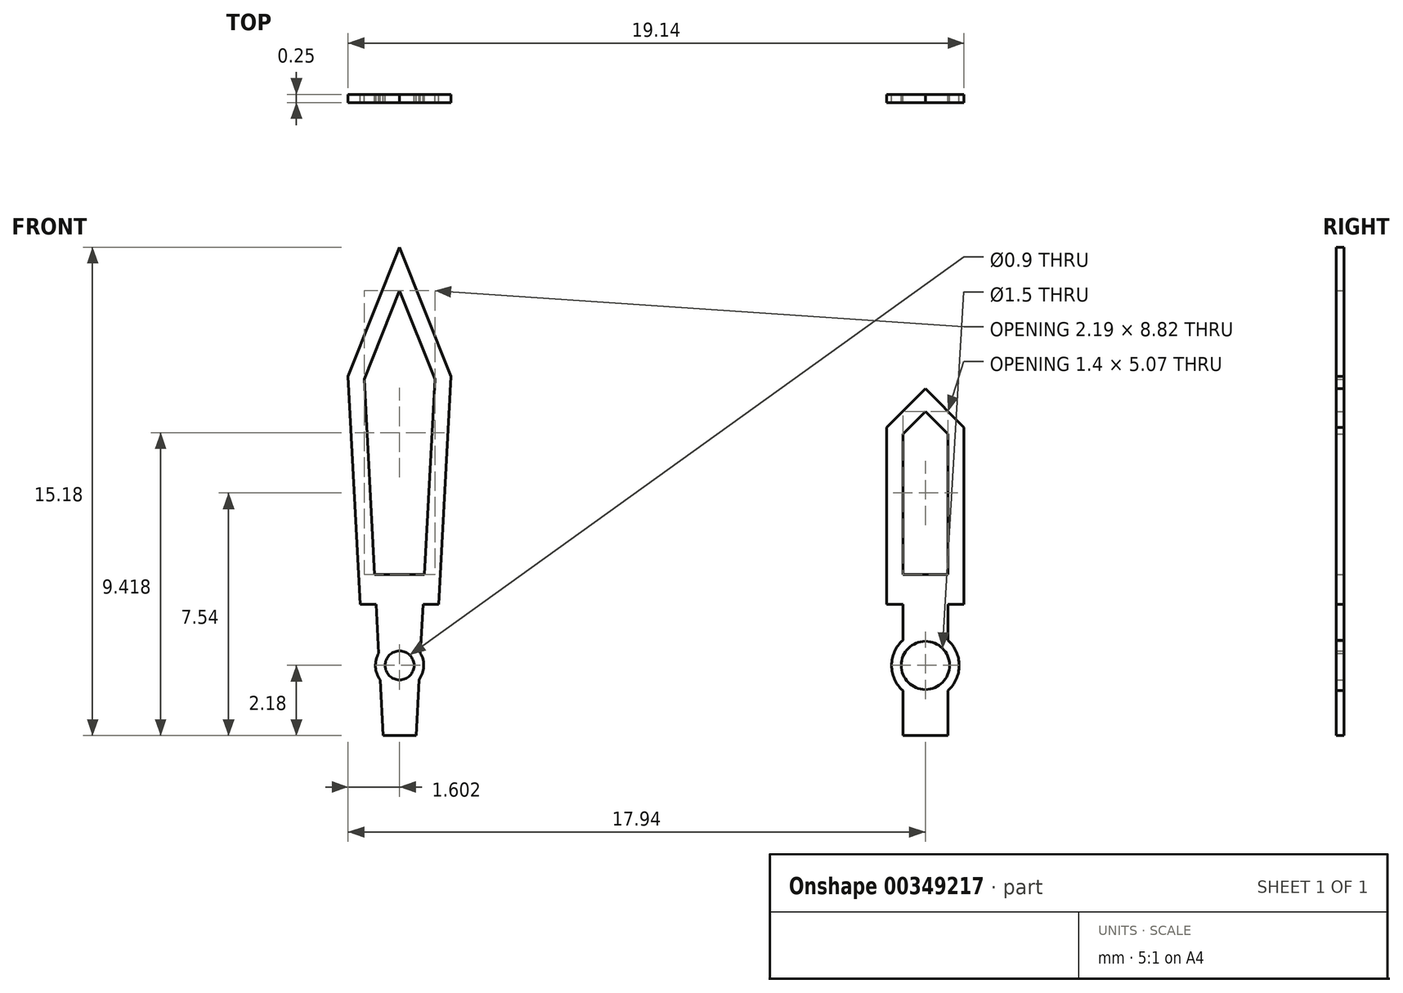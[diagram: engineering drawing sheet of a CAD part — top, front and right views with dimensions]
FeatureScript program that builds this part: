
annotation { "Feature Type Name" : "Feature", "Feature Type Description" : "" }
export const myFeature = defineFeature(function(context is Context, id is Id, definition is map)
    precondition{}
    {
        {
            var Q0;
            Q0=qCreatedBy(makeId("Front.planeOp"),FACE);
            var sketch = newSketch(context, id + "F0", { "sketchPlane" : qUnion([Q0])});
            skLineSegment(sketch, "E0", {"start": v(-36.59, 13) * mm, "end": v(-34.99, 8.98) * mm});
            skCircle(sketch, "E1", {"center": v(-36.59, 0) * mm, "radius": 0.45 * mm});
            skCircle(sketch, "E2.0", {"center": v(-36.59, 0) * mm, "radius": 0.75 * mm});
            skCircle(sketch, "E3", {"center": v(-20.25, 0) * mm, "radius": 0.75 * mm});
            skCircle(sketch, "E4", {"center": v(-20.25, 0) * mm, "radius": 1.05 * mm});
            skLineSegment(sketch, "E5", {"start": v(-36.59, 13) * mm, "end": v(-36.59, 0) * mm});
            skLineSegment(sketch, "E6.MirrorCS", {"start": v(-36.59, 13) * mm, "end": v(-38.19, 8.98) * mm});
            skLineSegment(sketch, "E7", {"start": v(-20.25, 8.6) * mm, "end": v(-20.25, 0) * mm});
            skLineSegment(sketch, "E8", {"start": v(-34.99, 8.98) * mm, "end": v(-35.58, -2.18) * mm});
            skLineSegment(sketch, "E9.MirrorCS", {"start": v(-38.19, 8.98) * mm, "end": v(-37.6, -2.18) * mm});
            skLineSegment(sketch, "E10", {"start": v(-19.05, 7.4) * mm, "end": v(-20.25, 8.6) * mm});
            skLineSegment(sketch, "E11", {"start": v(-20.25, 7.9) * mm, "end": v(-19.55, 7.2) * mm});
            skLineSegment(sketch, "E12.MirrorCS", {"start": v(-20.25, 7.9) * mm, "end": v(-20.95, 7.2) * mm});
            skLineSegment(sketch, "E13.MirrorCS", {"start": v(-21.45, 7.4) * mm, "end": v(-20.25, 8.6) * mm});
            skLineSegment(sketch, "E14", {"start": v(-36.59, 11.65) * mm, "end": v(-35.5, 8.9) * mm});
            skLineSegment(sketch, "E15", {"start": v(-35.5, 8.9) * mm, "end": v(-35.94, 0.38) * mm});
            skLineSegment(sketch, "E16.MirrorCS", {"start": v(-36.59, 11.65) * mm, "end": v(-37.68, 8.9) * mm});
            skLineSegment(sketch, "E17.MirrorCS", {"start": v(-37.68, 8.9) * mm, "end": v(-37.23, 0.38) * mm});
            skLineSegment(sketch, "E18", {"start": v(-19.05, 2.83) * mm, "end": v(-21.45, 2.83) * mm});
            skLineSegment(sketch, "E19.0", {"start": v(-19.05, -2.18) * mm, "end": v(-21.45, -2.18) * mm});
            skLineSegment(sketch, "E20", {"start": v(-21.45, 7.4) * mm, "end": v(-21.45, -2.18) * mm});
            skLineSegment(sketch, "E21", {"start": v(-20.95, 7.2) * mm, "end": v(-20.95, 0.27) * mm});
            skLineSegment(sketch, "E22", {"start": v(-19.05, 7.4) * mm, "end": v(-19.05, -2.18) * mm});
            skLineSegment(sketch, "E23", {"start": v(-19.55, 7.2) * mm, "end": v(-19.55, 0.27) * mm});
            skLineSegment(sketch, "E24.trimOffspring", {"start": v(-35.32, 2.83) * mm, "end": v(-37.86, 2.83) * mm});
            skLineSegment(sketch, "E25.trimOffspring", {"start": v(-35.58, -2.18) * mm, "end": v(-37.95, -2.18) * mm});
            skLineSegment(sketch, "E26.trimOffspring", {"start": v(-20.95, -0.27) * mm, "end": v(-20.95, -2.18) * mm});
            skLineSegment(sketch, "E27.trimOffspring", {"start": v(-19.55, -0.27) * mm, "end": v(-19.55, -2.18) * mm});
            skLineSegment(sketch, "E28.trimOffspring", {"start": v(-37.2, -0.45) * mm, "end": v(-37.1, -2.18) * mm});
            skLineSegment(sketch, "E29.trimOffspring", {"start": v(-35.99, -0.45) * mm, "end": v(-36.08, -2.18) * mm});
            skLineSegment(sketch, "E30.0", {"start": v(-35.58, -1.68) * mm, "end": v(-37.95, -1.68) * mm});
            skLineSegment(sketch, "E31.0", {"start": v(-19.05, -1.68) * mm, "end": v(-21.45, -1.68) * mm});
            skLineSegment(sketch, "E32", {"start": v(-19.05, 1.9) * mm, "end": v(-37.8, 1.9) * mm});
            skLineSegment(sketch, "E33", {"start": v(-35.32, 2.83) * mm, "end": v(-21.45, 2.83) * mm});
            skSolve(sketch);
        }
        {
            var Q0;
            {var subQ0=sQuery(id+"F0.wireOp",EDGE,"E28.trimOffspring");var subQ1=sQuery(id+"F0.wireOp",EDGE,"E25.trimOffspring");var subQ2=makeQuery(id+"F0.imprint","INTERSECT",VERTEX,{"derivedFrom":[subQ1,subQ0]});Q0=makeQuery(id+"F0.imprint","IMPRINT",FACE,{"disambiguationData":[TD([[makeQuery(id+"F0.imprint","IMPRINT",EDGE,{"disambiguationData":[TD([[subQ2,1.0]])],"derivedFrom":subQ1}),-1.0]])]});}
            var Q1;
            {var subQ2=sQuery(id+"F0.wireOp",EDGE,"E0");Q1=makeQuery(id+"F0.imprint","IMPRINT",FACE,{"disambiguationData":[TD([[makeQuery(id+"F0.imprint","IMPRINT",EDGE,{"derivedFrom":subQ2}),-1.0]])]});}
            var Q2;
            {var subQ0=sQuery(id+"F0.wireOp",EDGE,"E6.MirrorCS");Q2=makeQuery(id+"F0.imprint","IMPRINT",FACE,{"disambiguationData":[TD([[makeQuery(id+"F0.imprint","IMPRINT",EDGE,{"derivedFrom":subQ0}),1.0]])]});}
            var Q3;
            {var subQ5=sQuery(id+"F0.wireOp",EDGE,"E10");Q3=makeQuery(id+"F0.imprint","IMPRINT",FACE,{"disambiguationData":[TD([[makeQuery(id+"F0.imprint","IMPRINT",EDGE,{"derivedFrom":subQ5}),1.0]])]});}
            var Q4;
            {var subQ5=sQuery(id+"F0.wireOp",EDGE,"E12.MirrorCS");Q4=makeQuery(id+"F0.imprint","IMPRINT",FACE,{"disambiguationData":[TD([[makeQuery(id+"F0.imprint","IMPRINT",EDGE,{"derivedFrom":subQ5}),-1.0]])]});}
            var Q5;
            Q5=makeQuery(id+"F0.imprint","IMPRINT",FACE,{"disambiguationData":[TD([[makeQuery(id+"F0.imprint","IMPRINT",EDGE,{"derivedFrom":sQuery(id+"F0.wireOp",EDGE,"E1")}),-1.0]])]});
            var Q6;
            {var subQ0=sQuery(id+"F0.wireOp",EDGE,"E23");var subQ1=sQuery(id+"F0.wireOp",EDGE,"E3");var subQ2=makeQuery(id+"F0.imprint","INTERSECT",VERTEX,{"derivedFrom":[subQ1,subQ0]});Q6=makeQuery(id+"F0.imprint","IMPRINT",FACE,{"disambiguationData":[TD([[makeQuery(id+"F0.imprint","IMPRINT",EDGE,{"disambiguationData":[TD([[subQ2,-1.0]])],"derivedFrom":subQ1}),-1.0]])]});}
            var Q7;
            {var subQ0=sQuery(id+"F0.wireOp",EDGE,"E21");var subQ1=sQuery(id+"F0.wireOp",EDGE,"E3");var subQ2=makeQuery(id+"F0.imprint","INTERSECT",VERTEX,{"derivedFrom":[subQ1,subQ0]});Q7=makeQuery(id+"F0.imprint","IMPRINT",FACE,{"disambiguationData":[TD([[makeQuery(id+"F0.imprint","IMPRINT",EDGE,{"disambiguationData":[TD([[subQ2,1.0]])],"derivedFrom":subQ1}),-1.0]])]});}
            var Q8;
            {var subQ0=sQuery(id+"F0.wireOp",EDGE,"E21");var subQ1=sQuery(id+"F0.wireOp",EDGE,"E3");var subQ2=makeQuery(id+"F0.imprint","INTERSECT",VERTEX,{"derivedFrom":[subQ1,subQ0]});Q8=makeQuery(id+"F0.imprint","IMPRINT",FACE,{"disambiguationData":[TD([[makeQuery(id+"F0.imprint","IMPRINT",EDGE,{"disambiguationData":[TD([[subQ2,-1.0]])],"derivedFrom":subQ1}),-1.0]])]});}
            var Q9;
            {var subQ0=sQuery(id+"F0.wireOp",EDGE,"E26.trimOffspring");var subQ1=sQuery(id+"F0.wireOp",EDGE,"E3");var subQ2=makeQuery(id+"F0.imprint","INTERSECT",VERTEX,{"derivedFrom":[subQ1,subQ0]});Q9=makeQuery(id+"F0.imprint","IMPRINT",FACE,{"disambiguationData":[TD([[makeQuery(id+"F0.imprint","IMPRINT",EDGE,{"disambiguationData":[TD([[subQ2,-1.0]])],"derivedFrom":subQ1}),-1.0]])]});}
            var Q10;
            {var subQ0=sQuery(id+"F0.wireOp",EDGE,"E23");var subQ1=sQuery(id+"F0.wireOp",EDGE,"E3");var subQ2=makeQuery(id+"F0.imprint","INTERSECT",VERTEX,{"derivedFrom":[subQ1,subQ0]});Q10=makeQuery(id+"F0.imprint","IMPRINT",FACE,{"disambiguationData":[TD([[makeQuery(id+"F0.imprint","IMPRINT",EDGE,{"disambiguationData":[TD([[subQ2,1.0]])],"derivedFrom":subQ1}),-1.0]])]});}
            var Q11;
            {var subQ0=sQuery(id+"F0.wireOp",EDGE,"E26.trimOffspring");var subQ1=sQuery(id+"F0.wireOp",EDGE,"E19.0");var subQ2=makeQuery(id+"F0.imprint","INTERSECT",VERTEX,{"derivedFrom":[subQ1,subQ0]});Q11=makeQuery(id+"F0.imprint","IMPRINT",FACE,{"disambiguationData":[TD([[makeQuery(id+"F0.imprint","IMPRINT",EDGE,{"disambiguationData":[TD([[subQ2,1.0]])],"derivedFrom":subQ1}),-1.0]])]});}
            var Q12;
            {var subQ0=sQuery(id+"F0.wireOp",EDGE,"E28.trimOffspring");var subQ1=sQuery(id+"F0.wireOp",EDGE,"E2.0");var subQ2=makeQuery(id+"F0.imprint","INTERSECT",VERTEX,{"derivedFrom":[subQ1,subQ0]});Q12=makeQuery(id+"F0.imprint","IMPRINT",FACE,{"disambiguationData":[TD([[makeQuery(id+"F0.imprint","IMPRINT",EDGE,{"disambiguationData":[TD([[subQ2,-1.0]])],"derivedFrom":subQ1}),-1.0]])]});}
            var Q13;
            {var subQ0=sQuery(id+"F0.wireOp",EDGE,"E15");var subQ1=sQuery(id+"F0.wireOp",EDGE,"E2.0");var subQ2=makeQuery(id+"F0.imprint","INTERSECT",VERTEX,{"derivedFrom":[subQ1,subQ0]});Q13=makeQuery(id+"F0.imprint","IMPRINT",FACE,{"disambiguationData":[TD([[makeQuery(id+"F0.imprint","IMPRINT",EDGE,{"disambiguationData":[TD([[subQ2,-1.0]])],"derivedFrom":subQ1}),-1.0]])]});}
            var Q14;
            {var subQ0=sQuery(id+"F0.wireOp",EDGE,"E17.MirrorCS");var subQ1=sQuery(id+"F0.wireOp",EDGE,"E2.0");var subQ2=makeQuery(id+"F0.imprint","INTERSECT",VERTEX,{"derivedFrom":[subQ1,subQ0]});Q14=makeQuery(id+"F0.imprint","IMPRINT",FACE,{"disambiguationData":[TD([[makeQuery(id+"F0.imprint","IMPRINT",EDGE,{"disambiguationData":[TD([[subQ2,1.0]])],"derivedFrom":subQ1}),-1.0]])]});}
            var Q15;
            {var subQ0=sQuery(id+"F0.wireOp",EDGE,"E26.trimOffspring");var subQ1=sQuery(id+"F0.wireOp",EDGE,"E4");var subQ2=makeQuery(id+"F0.imprint","INTERSECT",VERTEX,{"derivedFrom":[subQ1,subQ0]});Q15=makeQuery(id+"F0.imprint","IMPRINT",FACE,{"disambiguationData":[TD([[makeQuery(id+"F0.imprint","IMPRINT",EDGE,{"disambiguationData":[TD([[subQ2,-1.0]])],"derivedFrom":subQ1}),-1.0]])]});}
            var Q16;
            {var subQ0=sQuery(id+"F0.wireOp",EDGE,"E7");var subQ1=sQuery(id+"F0.wireOp",EDGE,"E4");var subQ2=makeQuery(id+"F0.imprint","INTERSECT",VERTEX,{"derivedFrom":[subQ1,subQ0]});Q16=makeQuery(id+"F0.imprint","IMPRINT",FACE,{"disambiguationData":[TD([[makeQuery(id+"F0.imprint","IMPRINT",EDGE,{"disambiguationData":[TD([[subQ2,1.0]])],"derivedFrom":subQ1}),-1.0]])]});}
            var Q17;
            {var subQ0=sQuery(id+"F0.wireOp",EDGE,"E7");var subQ1=sQuery(id+"F0.wireOp",EDGE,"E4");var subQ2=makeQuery(id+"F0.imprint","INTERSECT",VERTEX,{"derivedFrom":[subQ1,subQ0]});Q17=makeQuery(id+"F0.imprint","IMPRINT",FACE,{"disambiguationData":[TD([[makeQuery(id+"F0.imprint","IMPRINT",EDGE,{"disambiguationData":[TD([[subQ2,-1.0]])],"derivedFrom":subQ1}),-1.0]])]});}
            var Q18;
            {var subQ0=sQuery(id+"F0.wireOp",EDGE,"E24.trimOffspring");var subQ1=sQuery(id+"F0.wireOp",EDGE,"E9.MirrorCS");var subQ2=makeQuery(id+"F0.imprint","INTERSECT",VERTEX,{"derivedFrom":[subQ1,subQ0]});Q18=makeQuery(id+"F0.imprint","IMPRINT",FACE,{"disambiguationData":[TD([[makeQuery(id+"F0.imprint","IMPRINT",EDGE,{"disambiguationData":[TD([[subQ2,-1.0]])],"derivedFrom":subQ1}),1.0]])]});}
            var Q19;
            {var subQ0=sQuery(id+"F0.wireOp",EDGE,"E24.trimOffspring");var subQ1=sQuery(id+"F0.wireOp",EDGE,"E5");var subQ2=makeQuery(id+"F0.imprint","INTERSECT",VERTEX,{"derivedFrom":[subQ1,subQ0]});Q19=makeQuery(id+"F0.imprint","IMPRINT",FACE,{"disambiguationData":[TD([[makeQuery(id+"F0.imprint","IMPRINT",EDGE,{"disambiguationData":[TD([[subQ2,-1.0]])],"derivedFrom":subQ1}),-1.0]])]});}
            var Q20;
            {var subQ0=sQuery(id+"F0.wireOp",EDGE,"E24.trimOffspring");var subQ1=sQuery(id+"F0.wireOp",EDGE,"E5");var subQ2=makeQuery(id+"F0.imprint","INTERSECT",VERTEX,{"derivedFrom":[subQ1,subQ0]});Q20=makeQuery(id+"F0.imprint","IMPRINT",FACE,{"disambiguationData":[TD([[makeQuery(id+"F0.imprint","IMPRINT",EDGE,{"disambiguationData":[TD([[subQ2,-1.0]])],"derivedFrom":subQ1}),1.0]])]});}
            var Q21;
            {var subQ0=sQuery(id+"F0.wireOp",EDGE,"E24.trimOffspring");var subQ1=sQuery(id+"F0.wireOp",EDGE,"E8");var subQ2=makeQuery(id+"F0.imprint","INTERSECT",VERTEX,{"derivedFrom":[subQ1,subQ0]});Q21=makeQuery(id+"F0.imprint","IMPRINT",FACE,{"disambiguationData":[TD([[makeQuery(id+"F0.imprint","IMPRINT",EDGE,{"disambiguationData":[TD([[subQ2,-1.0]])],"derivedFrom":subQ1}),-1.0]])]});}
            var Q22;
            {var subQ0=sQuery(id+"F0.wireOp",EDGE,"E20");var subQ1=sQuery(id+"F0.wireOp",EDGE,"E18");var subQ2=makeQuery(id+"F0.imprint","INTERSECT",VERTEX,{"derivedFrom":[subQ1,subQ0]});Q22=makeQuery(id+"F0.imprint","IMPRINT",FACE,{"disambiguationData":[TD([[makeQuery(id+"F0.imprint","IMPRINT",EDGE,{"disambiguationData":[TD([[subQ2,1.0]])],"derivedFrom":subQ1}),1.0]])]});}
            var Q23;
            {var subQ0=sQuery(id+"F0.wireOp",EDGE,"E22");var subQ1=sQuery(id+"F0.wireOp",EDGE,"E18");var subQ2=makeQuery(id+"F0.imprint","INTERSECT",VERTEX,{"derivedFrom":[subQ1,subQ0]});Q23=makeQuery(id+"F0.imprint","IMPRINT",FACE,{"disambiguationData":[TD([[makeQuery(id+"F0.imprint","IMPRINT",EDGE,{"disambiguationData":[TD([[subQ2,-1.0]])],"derivedFrom":subQ1}),1.0]])]});}
            var Q24;
            {var subQ0=sQuery(id+"F0.wireOp",EDGE,"E18");var subQ1=sQuery(id+"F0.wireOp",EDGE,"E7");var subQ2=makeQuery(id+"F0.imprint","INTERSECT",VERTEX,{"derivedFrom":[subQ1,subQ0]});Q24=makeQuery(id+"F0.imprint","IMPRINT",FACE,{"disambiguationData":[TD([[makeQuery(id+"F0.imprint","IMPRINT",EDGE,{"disambiguationData":[TD([[subQ2,-1.0]])],"derivedFrom":subQ1}),1.0]])]});}
            var Q25;
            {var subQ0=sQuery(id+"F0.wireOp",EDGE,"E18");var subQ1=sQuery(id+"F0.wireOp",EDGE,"E7");var subQ2=makeQuery(id+"F0.imprint","INTERSECT",VERTEX,{"derivedFrom":[subQ1,subQ0]});Q25=makeQuery(id+"F0.imprint","IMPRINT",FACE,{"disambiguationData":[TD([[makeQuery(id+"F0.imprint","IMPRINT",EDGE,{"disambiguationData":[TD([[subQ2,-1.0]])],"derivedFrom":subQ1}),-1.0]])]});}
            extrude(context, id + "F1", {"entities" : qUnion([Q0, Q1, Q2, Q3, Q4, Q5, Q6, Q7, Q8, Q9, Q10, Q11, Q12, Q13, Q14, Q15, Q16, Q17, Q18, Q19, Q20, Q21, Q22, Q23, Q24, Q25]), "depth" : .25 * mm});
        }
    });
